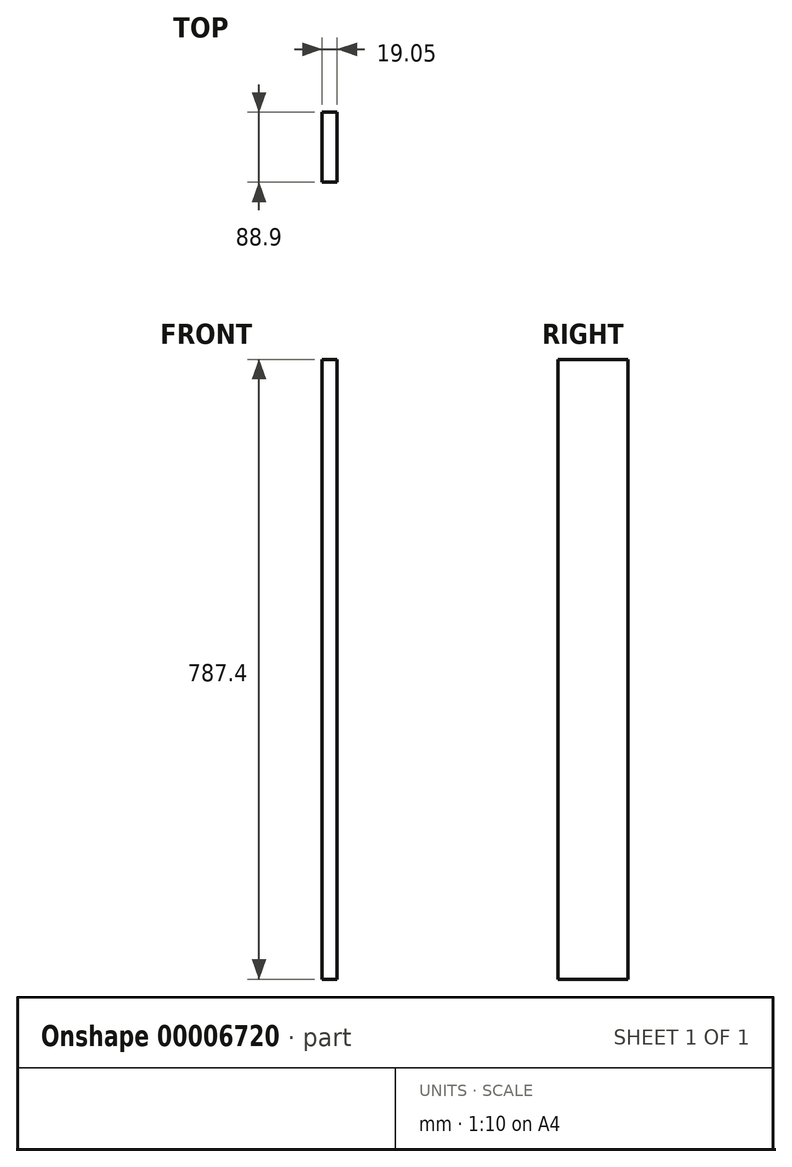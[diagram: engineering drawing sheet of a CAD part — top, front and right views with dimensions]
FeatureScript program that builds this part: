
annotation { "Feature Type Name" : "Feature", "Feature Type Description" : "" }
export const myFeature = defineFeature(function(context is Context, id is Id, definition is map)
    precondition{}
    {
        {
            var Q0;
            Q0=qCreatedBy(makeId("Top.planeOp"),FACE);
            var sketch = newSketch(context, id + "F0", { "sketchPlane" : qUnion([Q0])});
            skLineSegment(sketch, "E0.bottom", {"start": v(-9.4, 44.45) * mm, "end": v(9.65, 44.45) * mm});
            skLineSegment(sketch, "E0.top", {"start": v(-9.4, -44.45) * mm, "end": v(9.65, -44.45) * mm});
            skLineSegment(sketch, "E0.left", {"start": v(-9.4, 44.45) * mm, "end": v(-9.4, -44.45) * mm});
            skLineSegment(sketch, "E0.right", {"start": v(9.65, 44.45) * mm, "end": v(9.65, -44.45) * mm});
            skSolve(sketch);
        }
        {
            var Q0;
            Q0=qSketchRegion(id+"F0",true);
            extrude(context, id + "F1", {"entities" : qUnion([Q0]), "depth" : 787.4 * mm});
        }
    });
